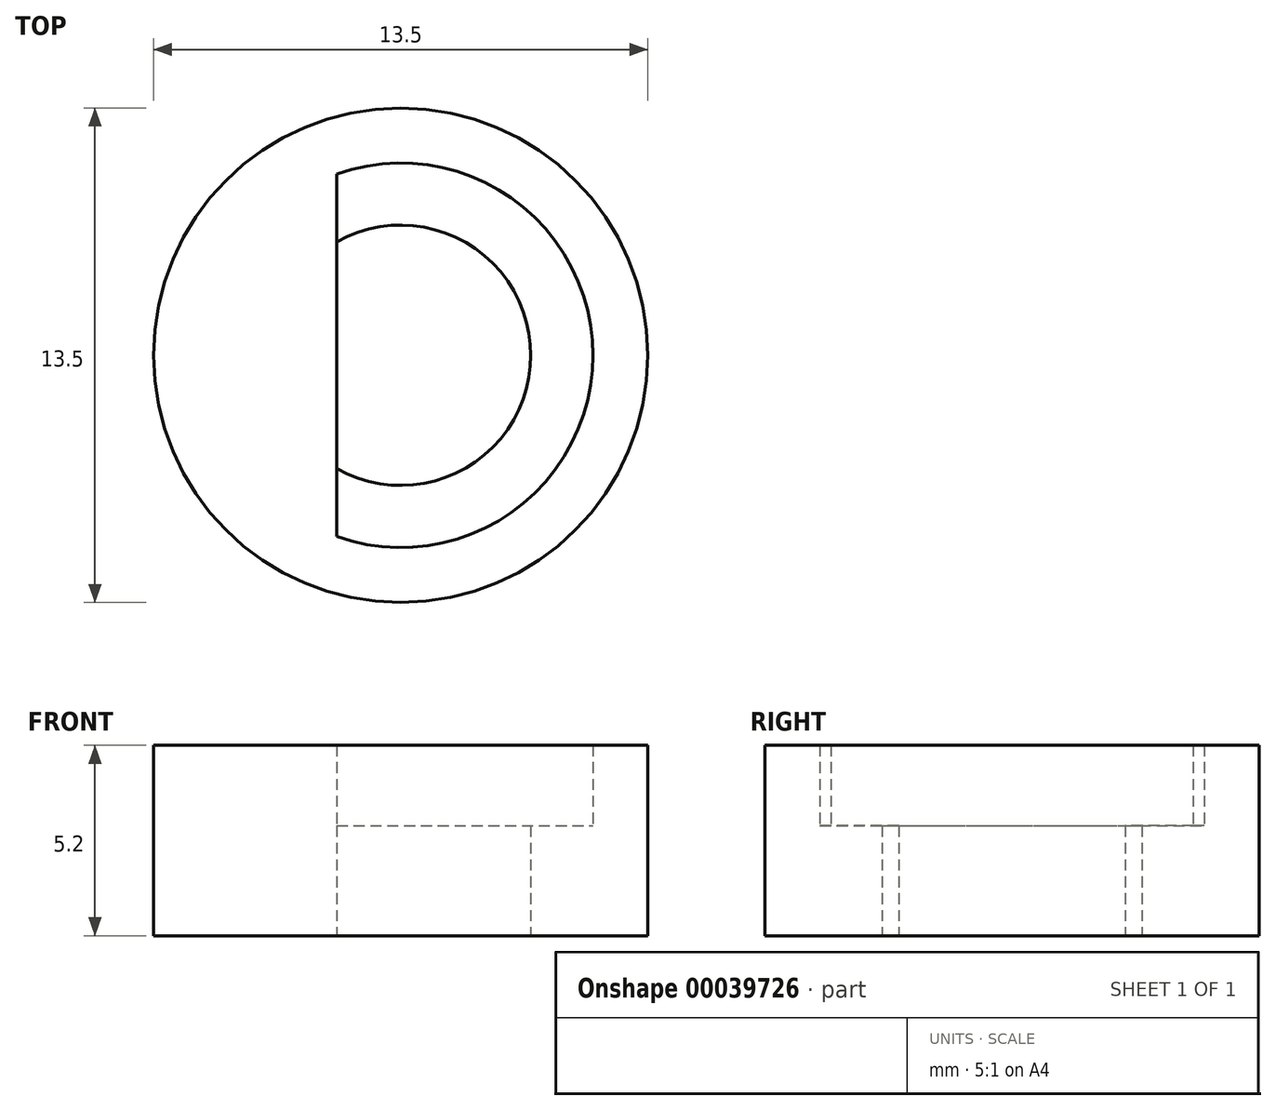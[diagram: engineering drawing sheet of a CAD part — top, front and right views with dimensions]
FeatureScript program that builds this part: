
annotation { "Feature Type Name" : "Feature", "Feature Type Description" : "" }
export const myFeature = defineFeature(function(context is Context, id is Id, definition is map)
    precondition{}
    {
        {
            var Q0;
            Q0=qCreatedBy(makeId("Top.planeOp"),FACE);
            var sketch = newSketch(context, id + "F0", { "sketchPlane" : qUnion([Q0])});
            skCircle(sketch, "E0", {"center": v(0, 0) * mm, "radius": 3.56 * mm});
            skCircle(sketch, "E1", {"center": v(0, 0) * mm, "radius": 5.25 * mm});
            skCircle(sketch, "E2", {"center": v(0, 0) * mm, "radius": 6.75 * mm});
            skLineSegment(sketch, "E3", {"start": v(3.56, 0) * mm, "end": v(-3.56, 0) * mm, "construction": true});
            skLineSegment(sketch, "E4", {"start": v(3.56, 0) * mm, "end": v(-1.74, 0) * mm});
            skLineSegment(sketch, "E5", {"start": v(-1.74, 4.95) * mm, "end": v(-1.74, -4.95) * mm});
            skSolve(sketch);
        }
        {
            var Q0;
            {var subQ1=sQuery(id+"F0.wireOp",EDGE,"E0");var subQ6=makeQuery(id+"F0.imprint","INTERSECT",VERTEX,{"derivedFrom":[subQ1,sQuery(id+"F0.wireOp",EDGE,"E4")]});Q0=makeQuery(id+"F0.imprint","IMPRINT",FACE,{"disambiguationData":[TD([[makeQuery(id+"F0.imprint","IMPRINT",EDGE,{"disambiguationData":[TD([[subQ6,-1.0]])],"derivedFrom":subQ1}),-1.0]])]});}
            extrude(context, id + "F1", {"entities" : qUnion([Q0]), "depth" : 3 * mm});
        }
        {
            var Q0;
            Q0=makeQuery(id+"F0.imprint","IMPRINT",FACE,{"disambiguationData":[TD([[makeQuery(id+"F0.imprint","IMPRINT",EDGE,{"derivedFrom":sQuery(id+"F0.wireOp",EDGE,"E2")}),1.0]])]});
            var Q1;
            {var subQ0=sQuery(id+"F0.wireOp",EDGE,"E5");var subQ1=sQuery(id+"F0.wireOp",EDGE,"E0");var subQ5=makeQuery(id+"F0.imprint","INTERSECT",VERTEX,{"disambiguationData":[OD(0.0)],"derivedFrom":[subQ1,subQ0]});Q1=makeQuery(id+"F0.imprint","IMPRINT",FACE,{"disambiguationData":[TD([[makeQuery(id+"F0.imprint","IMPRINT",EDGE,{"disambiguationData":[TD([[subQ5,-1.0]])],"derivedFrom":subQ1}),-1.0]])]});}
            var Q2;
            {var subQ0=sQuery(id+"F0.wireOp",EDGE,"E5");var subQ1=sQuery(id+"F0.wireOp",EDGE,"E0");var subQ4=makeQuery(id+"F0.imprint","INTERSECT",VERTEX,{"disambiguationData":[OD(0.0)],"derivedFrom":[subQ1,subQ0]});Q2=makeQuery(id+"F0.imprint","IMPRINT",FACE,{"disambiguationData":[TD([[makeQuery(id+"F0.imprint","IMPRINT",EDGE,{"disambiguationData":[TD([[subQ4,-1.0]])],"derivedFrom":subQ1}),1.0]])]});}
            extrude(context, id + "F2", {"entities" : qUnion([Q0, Q1, Q2]), "operationType" : NewBodyOperationType.ADD, "depth" : 5.2 * mm});
        }
    });
